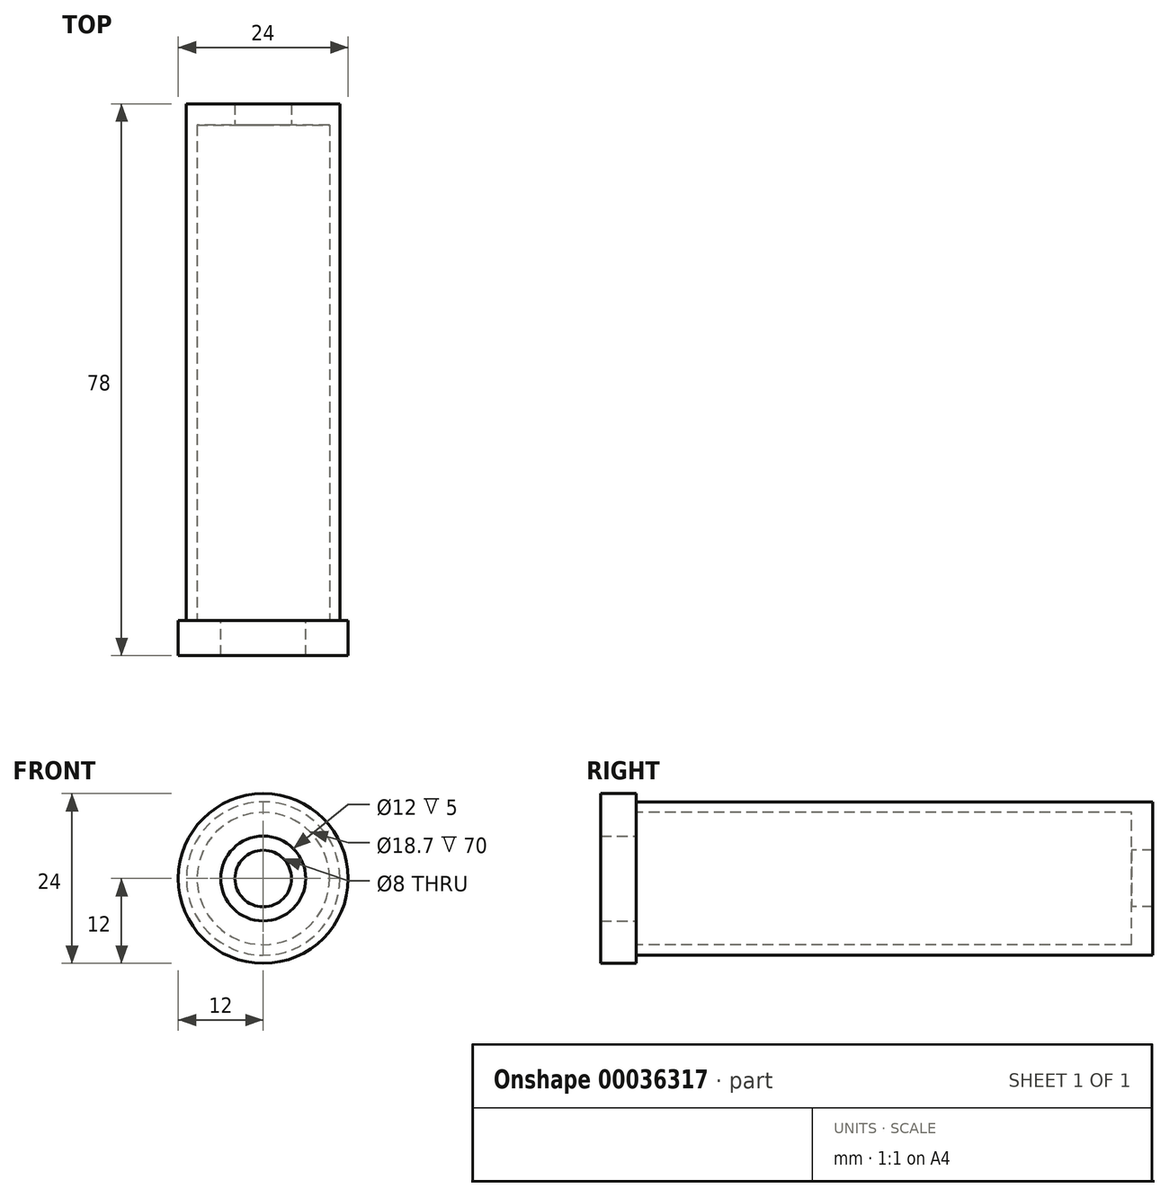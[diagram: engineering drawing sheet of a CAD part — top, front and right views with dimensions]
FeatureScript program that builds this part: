
annotation { "Feature Type Name" : "Feature", "Feature Type Description" : "" }
export const myFeature = defineFeature(function(context is Context, id is Id, definition is map)
    precondition{}
    {
        {
            var Q0;
            Q0=qCreatedBy(makeId("Front.planeOp"),FACE);
            var sketch = newSketch(context, id + "F0", { "sketchPlane" : qUnion([Q0])});
            skCircle(sketch, "E0", {"center": v(0, 0) * mm, "radius": 12 * mm});
            skCircle(sketch, "E1", {"center": v(0, 0) * mm, "radius": 10.85 * mm});
            skCircle(sketch, "E2", {"center": v(0, 0) * mm, "radius": 9.35 * mm});
            skCircle(sketch, "E3", {"center": v(0, 0) * mm, "radius": 6 * mm});
            skSolve(sketch);
        }
        {
            var Q0;
            Q0=makeQuery(id+"F0.imprint","IMPRINT",FACE,{"disambiguationData":[TD([[makeQuery(id+"F0.imprint","IMPRINT",EDGE,{"derivedFrom":sQuery(id+"F0.wireOp",EDGE,"E0")}),1.0]])]});
            var Q1;
            Q1=makeQuery(id+"F0.imprint","IMPRINT",FACE,{"disambiguationData":[TD([[makeQuery(id+"F0.imprint","IMPRINT",EDGE,{"derivedFrom":sQuery(id+"F0.wireOp",EDGE,"E1")}),1.0]])]});
            var Q2;
            Q2=makeQuery(id+"F0.imprint","IMPRINT",FACE,{"disambiguationData":[TD([[makeQuery(id+"F0.imprint","IMPRINT",EDGE,{"derivedFrom":sQuery(id+"F0.wireOp",EDGE,"E2")}),1.0]])]});
            extrude(context, id + "F1", {"entities" : qUnion([Q0, Q1, Q2]), "depth" : 5 * mm});
        }
        {
            var Q0;
            Q0=makeQuery(id+"F0.imprint","IMPRINT",FACE,{"disambiguationData":[TD([[makeQuery(id+"F0.imprint","IMPRINT",EDGE,{"derivedFrom":sQuery(id+"F0.wireOp",EDGE,"E1")}),1.0]])]});
            extrude(context, id + "F2", {"entities" : qUnion([Q0]), "operationType" : NewBodyOperationType.ADD, "oppositeDirection" : true, "depth" : 70 * mm});
        }
        {
            var Q0;
            Q0=makeQuery(id+"F2.opExtrude","CAP_FACE",FACE,{"disambiguationData":[OSD([sQuery(id+"F0.wireOp",EDGE,"E1"),sQuery(id+"F0.wireOp",EDGE,"E2")])],"isStart":false});
            var sketch = newSketch(context, id + "F3", { "sketchPlane" : qUnion([Q0])});
            skCircle(sketch, "E4", {"center": v(0, 0) * mm, "radius": 10.85 * mm});
            skCircle(sketch, "E5", {"center": v(0, 0) * mm, "radius": 4 * mm});
            skSolve(sketch);
        }
        {
            var Q0;
            Q0=qSketchRegion(id+"F3",true);
            extrude(context, id + "F4", {"entities" : qUnion([Q0]), "operationType" : NewBodyOperationType.ADD, "depth" : 3 * mm});
        }
    });
